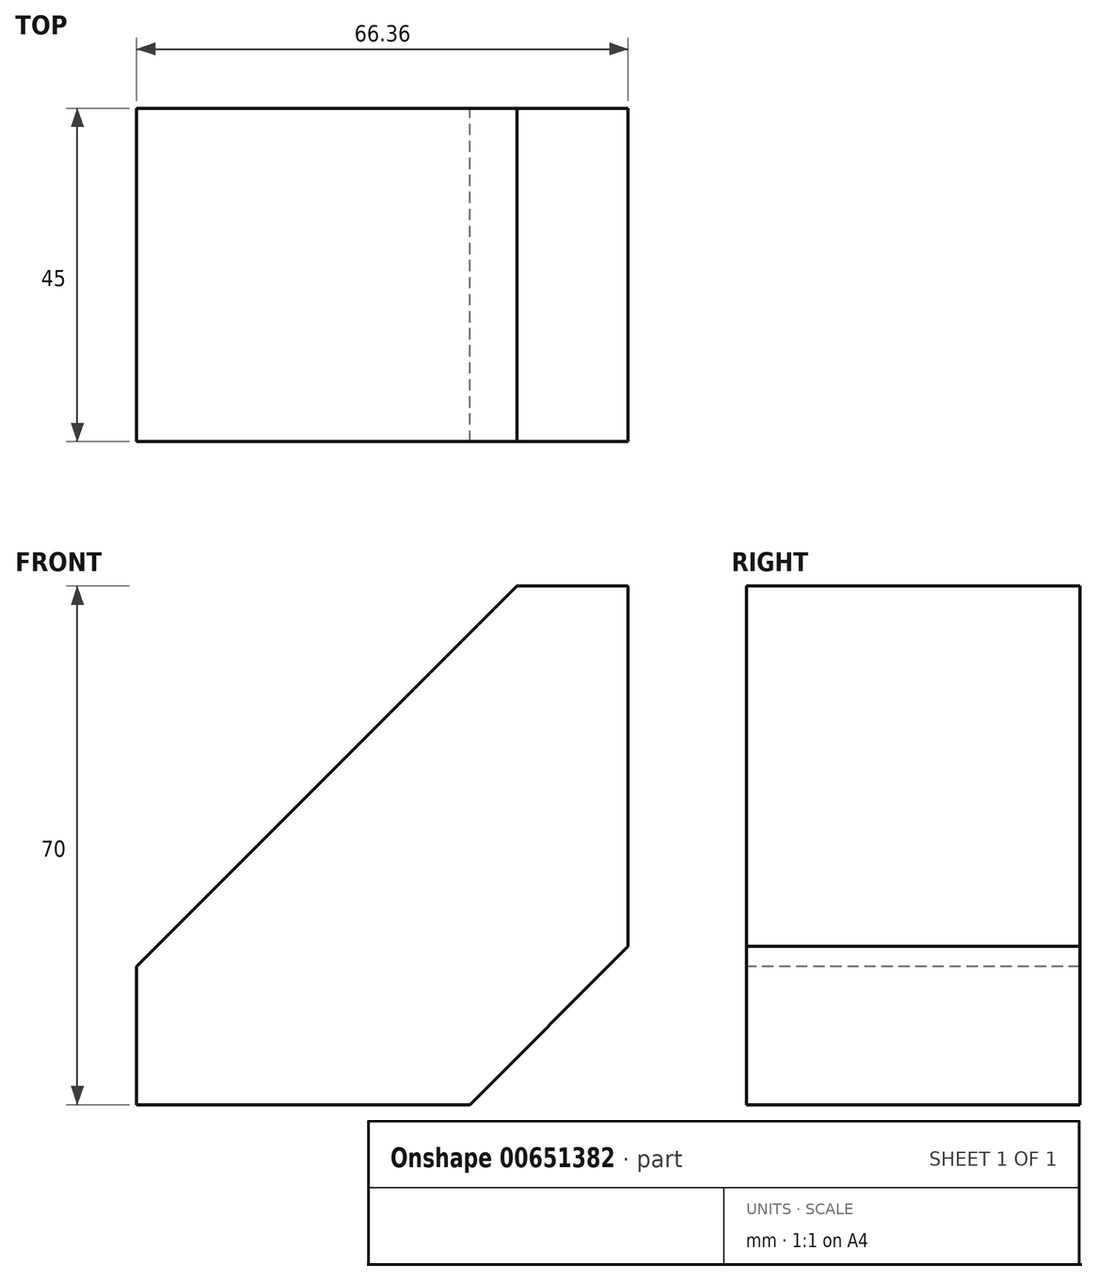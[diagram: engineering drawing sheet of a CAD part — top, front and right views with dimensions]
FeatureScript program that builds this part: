
annotation { "Feature Type Name" : "Feature", "Feature Type Description" : "" }
export const myFeature = defineFeature(function(context is Context, id is Id, definition is map)
    precondition{}
    {
        {
            var Q0;
            Q0=qCreatedBy(makeId("Front.planeOp"),FACE);
            var sketch = newSketch(context, id + "F0", { "sketchPlane" : qUnion([Q0])});
            skLineSegment(sketch, "E0", {"start": v(0, 0) * mm, "end": v(85, 85) * mm});
            skLineSegment(sketch, "E1", {"start": v(85, 85) * mm, "end": v(85, 21.36) * mm});
            skLineSegment(sketch, "E2", {"start": v(85, 21.36) * mm, "end": v(63.64, 0) * mm});
            skLineSegment(sketch, "E3", {"start": v(63.64, 0) * mm, "end": v(0, 0) * mm});
            skSolve(sketch);
        }
        {
            var Q0;
            Q0 = qSketchRegion(id + "F0", true);
            extrude(context, id + "F1", {"entities" : qUnion([Q0]), "depth" : 45 * mm, "offsetDistance" : 25 * mm});
        }
        {
            var Q0;
            Q0=makeQuery(id+"F1.opExtrude","CAP_FACE",FACE,{"disambiguationData":[OSD([sQuery(id+"F0.wireOp",EDGE,"E0"),sQuery(id+"F0.wireOp",EDGE,"E1"),sQuery(id+"F0.wireOp",EDGE,"E2"),sQuery(id+"F0.wireOp",EDGE,"E3")])],"isStart":false});
            var sketch = newSketch(context, id + "F2", { "sketchPlane" : qUnion([Q0])});
            skLineSegment(sketch, "E4", {"start": v(18.64, 0) * mm, "end": v(18.64, 18.64) * mm});
            skLineSegment(sketch, "E5", {"start": v(18.64, 18.64) * mm, "end": v(0, 0) * mm});
            skLineSegment(sketch, "E6", {"start": v(0, 0) * mm, "end": v(18.64, 0) * mm});
            skSolve(sketch);
        }
        {
            var Q0;
            Q0 = qSketchRegion(id + "F2", true);
            extrude(context, id + "F3", {"entities" : qUnion([Q0]), "operationType" : NewBodyOperationType.REMOVE, "endBound" : BoundingType.THROUGH_ALL, "oppositeDirection" : true, "depth" : 25 * mm, "offsetDistance" : 25 * mm});
        }
        {
            var Q0;
            Q0=makeQuery(id+"F1.opExtrude","CAP_FACE",FACE,{"disambiguationData":[OSD([sQuery(id+"F0.wireOp",EDGE,"E0"),sQuery(id+"F0.wireOp",EDGE,"E1"),sQuery(id+"F0.wireOp",EDGE,"E2"),sQuery(id+"F0.wireOp",EDGE,"E3")])],"isStart":false});
            var sketch = newSketch(context, id + "F4", { "sketchPlane" : qUnion([Q0])});
            skLineSegment(sketch, "E7", {"start": v(70, 70) * mm, "end": v(85, 70) * mm});
            skLineSegment(sketch, "E8", {"start": v(85, 70) * mm, "end": v(85, 85) * mm});
            skLineSegment(sketch, "E9", {"start": v(85, 85) * mm, "end": v(70, 70) * mm});
            skSolve(sketch);
        }
        {
            var Q0;
            Q0 = qSketchRegion(id + "F4", true);
            extrude(context, id + "F5", {"entities" : qUnion([Q0]), "operationType" : NewBodyOperationType.REMOVE, "endBound" : BoundingType.THROUGH_ALL, "oppositeDirection" : true, "depth" : 25 * mm, "offsetDistance" : 25 * mm});
        }
    });
